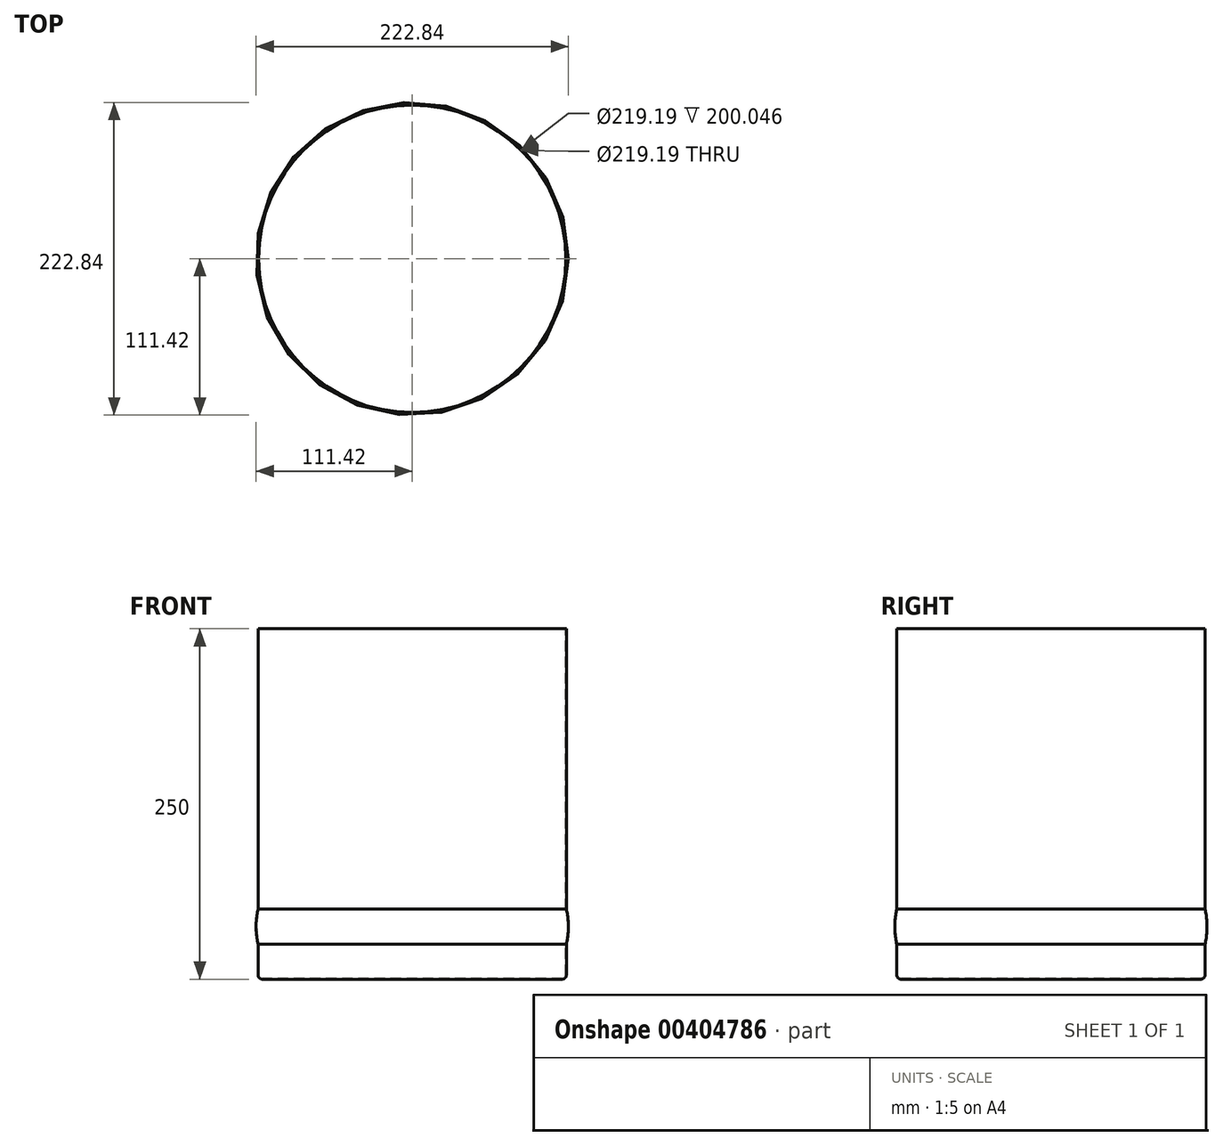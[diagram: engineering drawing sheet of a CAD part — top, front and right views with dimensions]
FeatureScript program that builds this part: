
annotation { "Feature Type Name" : "Feature", "Feature Type Description" : "" }
export const myFeature = defineFeature(function(context is Context, id is Id, definition is map)
    precondition{}
    {
        {
            var Q0;
            Q0=qCreatedBy(makeId("Right.planeOp"),FACE);
            var sketch = newSketch(context, id + "F0", { "sketchPlane" : qUnion([Q0])});
            skLineSegment(sketch, "E0", {"start": v(0, 0) * mm, "end": v(107, 0) * mm});
            skLineSegment(sketch, "E1", {"start": v(110, 3) * mm, "end": v(110, 25) * mm});
            skArc(sketch, "E2", {"start": v(110, 25) * mm, "mid": v(111.42, 37.5) * mm, "end": v(110, 50) * mm});
            skPoint(sketch, "E3.end.orphan", {"position": v(110, 34.94) * mm});
            skLineSegment(sketch, "E4.trimOffspring", {"start": v(110, 50) * mm, "end": v(110, 250) * mm});
            skLineSegment(sketch, "E5.0", {"start": v(109.6, 49.95) * mm, "end": v(109.6, 250) * mm});
            skArc(sketch, "E5.1", {"start": v(109.6, 25.05) * mm, "mid": v(111.02, 37.5) * mm, "end": v(109.6, 49.95) * mm});
            skLineSegment(sketch, "E5.2", {"start": v(109.6, 3) * mm, "end": v(109.6, 25.05) * mm});
            skLineSegment(sketch, "E5.3", {"start": v(0, 0.4) * mm, "end": v(107, 0.4) * mm});
            skLineSegment(sketch, "E6", {"start": v(109.6, 250) * mm, "end": v(110, 250) * mm});
            skLineSegment(sketch, "E7", {"start": v(0, 0.4) * mm, "end": v(0, 0) * mm});
            skPoint(sketch, "E8.visualSharp", {"position": v(110, 0) * mm});
            skArc(sketch, "E8.filletArc", {"start": v(107, 0) * mm, "mid": v(109.12, 0.88) * mm, "end": v(110, 3) * mm});
            skPoint(sketch, "E9.visualSharp", {"position": v(109.6, 0.4) * mm});
            skArc(sketch, "E9.filletArc", {"start": v(107, 0.4) * mm, "mid": v(108.84, 1.16) * mm, "end": v(109.6, 3) * mm});
            skSolve(sketch);
        }
        {
            var Q0;
            Q0=makeQuery(id+"F0.imprint","IMPRINT",FACE,{"disambiguationData":[TD([[makeQuery(id+"F0.imprint","IMPRINT",EDGE,{"derivedFrom":sQuery(id+"F0.wireOp",EDGE,"E0")}),1.0]])]});
            var Q1;
            Q1=sQuery(id+"F0.wireOp",EDGE,"E7");
            revolve(context, id + "F1", {"entities" : qUnion([Q0]), "axis" : qUnion([Q1]), "revolveType" : RevolveType.FULL});
        }
    });
